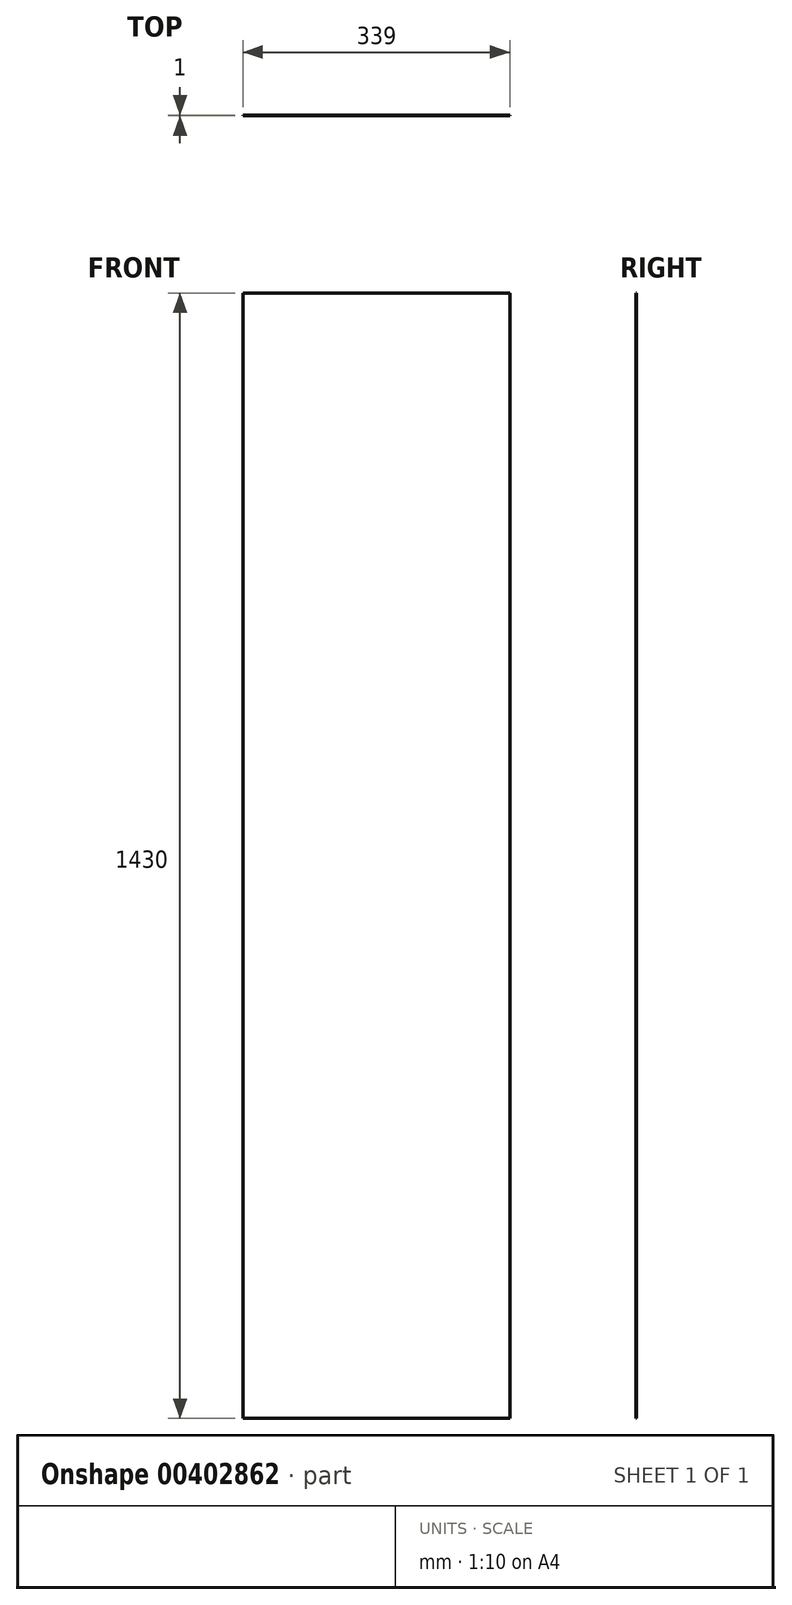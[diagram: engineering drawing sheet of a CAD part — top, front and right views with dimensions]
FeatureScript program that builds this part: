
annotation { "Feature Type Name" : "Feature", "Feature Type Description" : "" }
export const myFeature = defineFeature(function(context is Context, id is Id, definition is map)
    precondition{}
    {
        {
            var Q0;
            Q0=qCreatedBy(makeId("Front.planeOp"),FACE);
            var sketch = newSketch(context, id + "F0", { "sketchPlane" : qUnion([Q0])});
            skLineSegment(sketch, "E0.bottom", {"start": v(-169.5, 715) * mm, "end": v(169.5, 715) * mm});
            skLineSegment(sketch, "E0.top", {"start": v(-169.5, -715) * mm, "end": v(169.5, -715) * mm});
            skLineSegment(sketch, "E0.left", {"start": v(-169.5, 715) * mm, "end": v(-169.5, -715) * mm});
            skLineSegment(sketch, "E0.right", {"start": v(169.5, 715) * mm, "end": v(169.5, -715) * mm});
            skPoint(sketch, "E0.middle", {"position": v(0, 0) * mm});
            skSolve(sketch);
        }
        {
            var Q0;
            Q0=makeQuery(id+"F0.imprint","IMPRINT",FACE,{"disambiguationData":[TD([[makeQuery(id+"F0.imprint","IMPRINT",EDGE,{"derivedFrom":sQuery(id+"F0.wireOp",EDGE,"E0.bottom")}),-1.0]])]});
            extrude(context, id + "F1", {"entities" : qUnion([Q0]), "depth" : 1 * mm});
        }
    });
